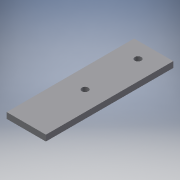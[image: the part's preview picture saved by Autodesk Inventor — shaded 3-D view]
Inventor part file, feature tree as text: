
AUTODESK INVENTOR PART (.ipt)
format: ipt  version: 2016 (Build 200138000, 138)  size: 93,184 bytes
history: native  units: mm
features: extrude x2, sketch x2, reference x2
ambient origin geometry x8: Origin, YZ Plane, XZ Plane, XY Plane, X Axis, Y Axis, Z Axis, Center Point
bodies: Solid1 (feature_tree)
feature tree (6):
  extrude  "Extrusion1"  Depth=130.0mm
  extrude  "Extrusion2"  Depth=6.0mm TaperAngle=0.0deg
  sketch  "Sketch1"  dims[d0=40.0mm d1=130.0mm]
  sketch  "Sketch2"  dims[d2=6.0mm d3=0.0mm d4=6.0mm d5=0.0mm]
  reference  "Reference1"
  reference  "Reference2"
